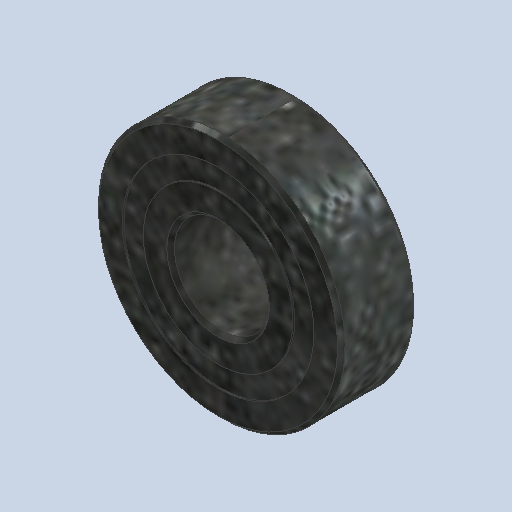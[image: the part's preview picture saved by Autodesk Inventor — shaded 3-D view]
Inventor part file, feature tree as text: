
AUTODESK INVENTOR PART (.ipt)
format: ipt  version: 2023 (Build 270158030, 158C)  size: 599,040 bytes
history: mixed  units: in
note: dims shown in document units (in); Inventor stores cm internally (conversion verified against a paired STEP export)
features: other x9, revolve x5, imported_body x1
ambient origin geometry x8: Origin, YZ Plane, XZ Plane, XY Plane, X Axis, Y Axis, Z Axis, Center Point
bodies: Solid1 (imported_parasolid), Solid2 (imported_parasolid), Solid3 (imported_parasolid), Solid4 (imported_parasolid), Solid5 (imported_parasolid), Solid6 (imported_parasolid), Solid7 (imported_parasolid), Solid8 (imported_parasolid), Solid9 (imported_parasolid), Solid10 (imported_parasolid), Solid11 (imported_parasolid), Solid12 (imported_parasolid), Solid13 (imported_parasolid), Solid14 (imported_parasolid)
feature tree (15):
  revolve  "Revolve6"  [1 undecoded]
  revolve  "Revolve3"  [1 undecoded]
  revolve  "Revolve4"  [1 undecoded]
  other  "CirPattern1[1]"
  other  "CirPattern1[2]"
  other  "CirPattern1[3]"
  other  "CirPattern1[4]"
  other  "CirPattern1[5]"
  other  "CirPattern1[6]"
  other  "CirPattern1[7]"
  other  "CirPattern1[8]"
  other  "CirPattern1[9]"
  revolve  "Revolve5[1]"  [1 undecoded]
  revolve  "Revolve5[2]"  [1 undecoded]
  imported_body  NMx_Import_Brep_tag  [imported B-rep: ~34 faces, bbox_mm=[0.0, 8.0, 8.0]]
note: 5 required parameter values undecoded (feature->parameter linkage not recoverable at this tier; creation-order binding heuristic only, values carry confidence <= 0.55)
